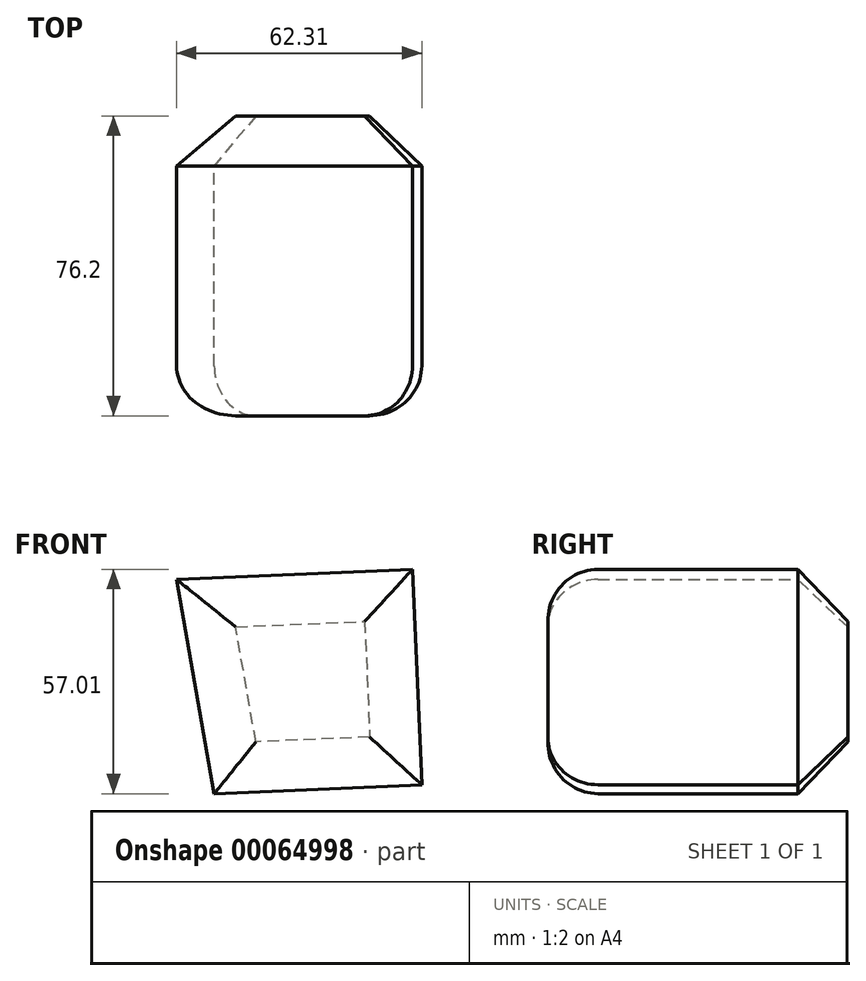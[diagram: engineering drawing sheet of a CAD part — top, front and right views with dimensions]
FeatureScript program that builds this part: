
annotation { "Feature Type Name" : "Feature", "Feature Type Description" : "" }
export const myFeature = defineFeature(function(context is Context, id is Id, definition is map)
    precondition{}
    {
        {
            var Q0;
            Q0=qCreatedBy(makeId("Front.planeOp"),FACE);
            var sketch = newSketch(context, id + "F0", { "sketchPlane" : qUnion([Q0])});
            skLineSegment(sketch, "E0", {"start": v(-24.85, 25.17) * mm, "end": v(35.11, 27.74) * mm});
            skLineSegment(sketch, "E1", {"start": v(35.11, 27.74) * mm, "end": v(37.46, -27.01) * mm});
            skLineSegment(sketch, "E2", {"start": v(37.46, -27.01) * mm, "end": v(-15.26, -29.27) * mm});
            skLineSegment(sketch, "E3", {"start": v(-15.26, -29.27) * mm, "end": v(-24.85, 25.17) * mm});
            skSolve(sketch);
        }
        {
            var Q0;
            Q0 = qSketchRegion(id + "F0", true);
            extrude(context, id + "F1", {"entities" : qUnion([Q0]), "depth" : 76.2 * mm});
        }
        {
            var Q0;
            Q0=makeQuery(id+"F1.opExtrude","CAP_EDGE",EDGE,{"disambiguationData":[OSD([sQuery(id+"F0.wireOp",EDGE,"E0")])],"isStart":false});
            var Q1;
            Q1=makeQuery(id+"F1.opExtrude","CAP_EDGE",EDGE,{"disambiguationData":[OSD([sQuery(id+"F0.wireOp",EDGE,"E1")])],"isStart":false});
            var Q2;
            Q2=makeQuery(id+"F1.opExtrude","CAP_EDGE",EDGE,{"disambiguationData":[OSD([sQuery(id+"F0.wireOp",EDGE,"E2")])],"isStart":false});
            var Q3;
            Q3=makeQuery(id+"F1.opExtrude","CAP_EDGE",EDGE,{"disambiguationData":[OSD([sQuery(id+"F0.wireOp",EDGE,"E3")])],"isStart":false});
            fillet(context, id + "F2", {"entities" : qUnion([Q0, Q1, Q2, Q3]), "radius" : 12.7 * mm, "tangentPropagation" : true, "allowEdgeOverflow" : false});
        }
        {
            var Q0;
            Q0=makeQuery(id+"F1.opExtrude","CAP_EDGE",EDGE,{"disambiguationData":[OSD([sQuery(id+"F0.wireOp",EDGE,"E2")])],"isStart":true});
            var Q1;
            Q1=makeQuery(id+"F1.opExtrude","CAP_EDGE",EDGE,{"disambiguationData":[OSD([sQuery(id+"F0.wireOp",EDGE,"E0")])],"isStart":true});
            var Q2;
            Q2=makeQuery(id+"F1.opExtrude","CAP_EDGE",EDGE,{"disambiguationData":[OSD([sQuery(id+"F0.wireOp",EDGE,"E1")])],"isStart":true});
            var Q3;
            Q3=makeQuery(id+"F1.opExtrude","CAP_EDGE",EDGE,{"disambiguationData":[OSD([sQuery(id+"F0.wireOp",EDGE,"E3")])],"isStart":true});
            chamfer(context, id + "F3", {"entities" : qUnion([Q0, Q1, Q2, Q3]), "width" : 12.7 * mm, "tangentPropagation" : true});
        }
    });
